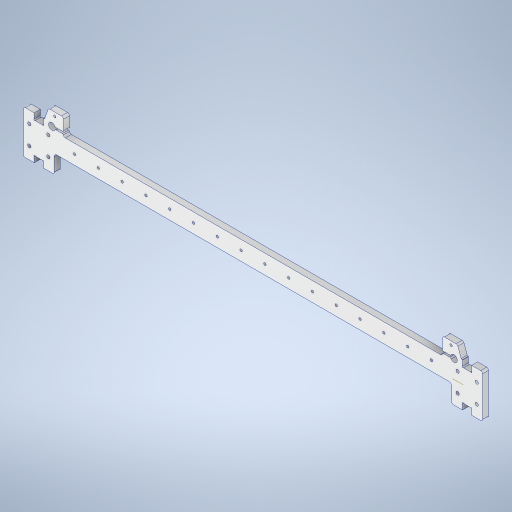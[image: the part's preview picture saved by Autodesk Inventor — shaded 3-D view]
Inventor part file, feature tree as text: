
AUTODESK INVENTOR PART (.ipt)
format: ipt  version: 2024 (Build 280153000, 153)  size: 691,712 bytes
history: native  units: mm
features: extrude x7, sketch x7, fillet x7, mirror x6, projected_geometry x5, hole x3, plane x3
ambient origin geometry x8: Origin, YZ Plane, XZ Plane, XY Plane, X Axis, Y Axis, Z Axis, Center Point
bodies: Solid1 (feature_tree)
feature tree (38):
  extrude  "Extrusion1"  Depth=450.0mm
  hole  "Hole1"  [1 undecoded]
  extrude  "Extrusion2"  Depth=20.0mm
  hole  "Hole2"  [1 undecoded]
  sketch  "Sketch5"  dims[d11=20.0mm]
  extrude  "Extrusion3"  Depth=2.0mm
  extrude  "Extrusion4"  Depth=1.0mm
  fillet  "Fillet1"  Radius=6.35mm
  mirror  "Mirror1"
  sketch  "Sketch7"  dims[d12=3.3mm d13=6.0mm d14=4.0mm d15=2.0mm d16=90.0deg d17=8.0mm d18=20.594885mm d19=6.2mm]
  extrude  "Extrusion5"  Depth=10.0mm
  extrude  "Extrusion6"  Depth=2.0mm
  mirror  "Mirror2"
  extrude  "Extrusion7"  Depth=4.5mm
  plane  "Work Plane1"
  mirror  "Mirror3"
  plane  "Work Plane2"
  mirror  "Mirror4"
  mirror  "Mirror5"
  hole  "Hole3"  [1 undecoded]
  mirror  "Mirror6"
  fillet  "Fillet3"  Radius=12.0mm
  fillet  "Fillet4"  Radius=18.0mm
  fillet  "Fillet5"  Radius=42.0mm
  fillet  "Fillet6"  Radius=10.0mm
  fillet  "Fillet7"  [1 undecoded]
  fillet  "Fillet8"  Radius=2.0mm
  plane  "Work Plane3"
  sketch  "Sketch1"  dims[d0=450.0mm d1=27.0mm]
  sketch  "Sketch2"  dims[d2=32.4mm d3=20.0mm]
  sketch  "Sketch3"  dims[d6=6.35mm d7=0.0mm d8=20.0mm]
  projected_geometry  "Projected Loop1"
  sketch  "Sketch4"  dims[d9=20.0mm d10=20.0mm]
  projected_geometry  "Projected Loop2"
  projected_geometry  "Projected Loop3"
  projected_geometry  "Projected Loop5"
  sketch  "Sketch8"  dims[d20=6.2mm d21=6.2mm d22=6.2mm d23=6.35mm d24=0.0mm d32=2.459mm d33=6.0mm d34=4.0mm d35=2.0mm d36=90.0deg d37=8.0mm d38=20.594885mm d39=160.0mm d41=25.0mm d42=10.0mm d44=10.0mm d46=2.0mm d47=4.5mm d48=7.0mm d49=12.0mm d50=18.0mm d51=42.0mm d52=10.0mm d53=0.0mm d54=0.0mm d55=0.0mm d56=2.0mm d59=33.0mm d60=4.0mm d61=15.0mm d62=7.0mm d63=9.525mm d64=45.4mm d65=6.0mm d68=5.0mm d69=10.0mm d70=0.0mm d71=10.0mm d72=0.0mm d74=19.198622mm d75=4.0mm d76=19.198622mm d77=1.5mm d78=0.4mm d80=0.0mm d81=0.0mm d82=0.4mm d83=2.459mm d84=6.0mm d85=4.0mm d86=2.0mm d87=90.0deg d88=8.0mm d89=0.0mm d90=2.0mm d91=3.0mm d92=2.0mm d93=1.0mm d94=2.0mm d95=1.0mm d96=-23.5mm]
  projected_geometry  "Projected Loop6"
note: 4 required parameter values undecoded (feature->parameter linkage not recoverable at this tier; creation-order binding heuristic only, values carry confidence <= 0.55)
